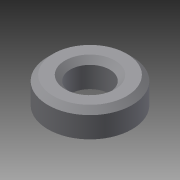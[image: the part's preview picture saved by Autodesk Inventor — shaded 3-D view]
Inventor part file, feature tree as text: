
AUTODESK INVENTOR PART (.ipt)
format: ipt  version: 2014 (Build 180170000, 170)  size: 90,624 bytes
history: native  units: mm
features: extrude x2, chamfer x2, sketch x2
ambient origin geometry x8: Origin, YZ Plane, XZ Plane, XY Plane, X Axis, Y Axis, Z Axis, Center Point
bodies: Solid1 (feature_tree)
feature tree (6):
  extrude  "Extrusion1"  Depth=5.0mm TaperAngle=0.0deg
  extrude  "Extrusion2"  Depth=5.0mm TaperAngle=0.0deg
  chamfer  "Chamfer1"  Distance=1.0mm Angle=45.0deg
  chamfer  "Chamfer2"  Distance=1.0mm Angle=45.0deg
  sketch  "Sketch1"  dims[d0=16.0mm d1=5.0mm d2=0.0mm]
  sketch  "Sketch2"  dims[d3=7.5mm d4=5.0mm d5=0.0mm d6=1.0mm d7=2.0mm d8=45.0deg d9=1.0mm d10=2.0mm d11=45.0deg]
